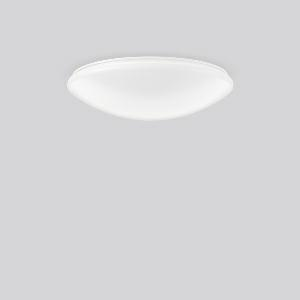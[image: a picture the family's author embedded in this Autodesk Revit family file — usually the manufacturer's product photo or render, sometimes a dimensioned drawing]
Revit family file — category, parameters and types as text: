
# Revit family: flat_polymero_312244_002_2_76_fe0a
name_source: partatom
category: Lighting Fixtures
units: mm (PartAtom-declared; Revit-internal decimal feet)

## family parameters
Cut with Voids When Loaded = No
Host = Face
Light Source = No
Part Type = Normal
Room Calculation Point = No
Round Connector Dimension = Use Diameter
Shared = No

## types (1)
- FLAT POLYMERO (1 x LED Modul 830, 3300 lm, 3000)
    Apparent Load = 32 VA
    CIE Flux Codes = 41 71 89 89 100
    Color Rendering = 80
    Color Temperature = 3000
    Default Elevation = 1800 mm
    Description = Series: FLAT POLYMERO
Decorative round surface-mounted luminaire. Base: metal, powder-coated. Diffuser made of plastic (polycarbonate), opal, shockproof. Diffuser fastening: patented push system. Suitable for Ceiling mounting, Wall (surface). 
Colour: white
Diameter: 460 mm
Height: 120 mm
Lamp: LED exchangeable
Socket: without socket
Colour temperature: 3000K
Colour rendering index (CRI): 83
System power: 32 W
Rated luminous flux: 3300 lm
Beam angle Down: 119°
Luminous efficiency: 103 lm/W
Control gear: AC power, DALI dimmable
Protection class: I
Type of protection: IP 40
    Height = 120 mm
    Lamp = 1 x LED Modul 830
    Lamp Light Flux = 3300 lm
    Lamp count = 1
    Length = 460 mm
    Lifetime = 50000 h
    Luminous efficacy = 103 lm/W
    Manufacturer = RZB
    ModVariant = No
    Model = 312244.002.2.76
    Mounting Place = Ceiling, Wall
    Mounting Type = Surface mounted
    Number of Poles = 1
    OnlyDefault = Yes
    Power Factor = 1
    Product Name = FLAT POLYMERO
    Product group = Surface mounted ceiling and wall luminaires
    ProductGroupID = 305
    Protection Class = Protection class I
    Protection Degree = IP 40
    RLX_Detail_Level = 1
    RLX_Emergency_Light_Flux = 0 lm
    RLX_Emergency_Type = 0
    RLX_Emergency_Type_DB = No
    RlxData = <blob elided: 75789 chars, md5=7de1bbbf>
    Socket = socket
    Standby Power = 0 W
    System Light Flux = 3300 lm
    System Power = 32 W
    Type Comments = ALEA SPOT
    Type Image = 311518.002.1.jpg
    URL = http://relux.com
    VarID = ---
    Voltage = 230 V
    Voltage Range = 220-240 V
    Weight = 0.00 kg
    Width = 0 mm  [stored 0 ft]

note: [stored X ft] marks values corroborated as IEEE doubles in the binary element streams (Revit-internal decimal feet)

## geometry (parser evidence)
native form markers: Blend x4, Sweep x12
no freeform markers — native parametric forms only
